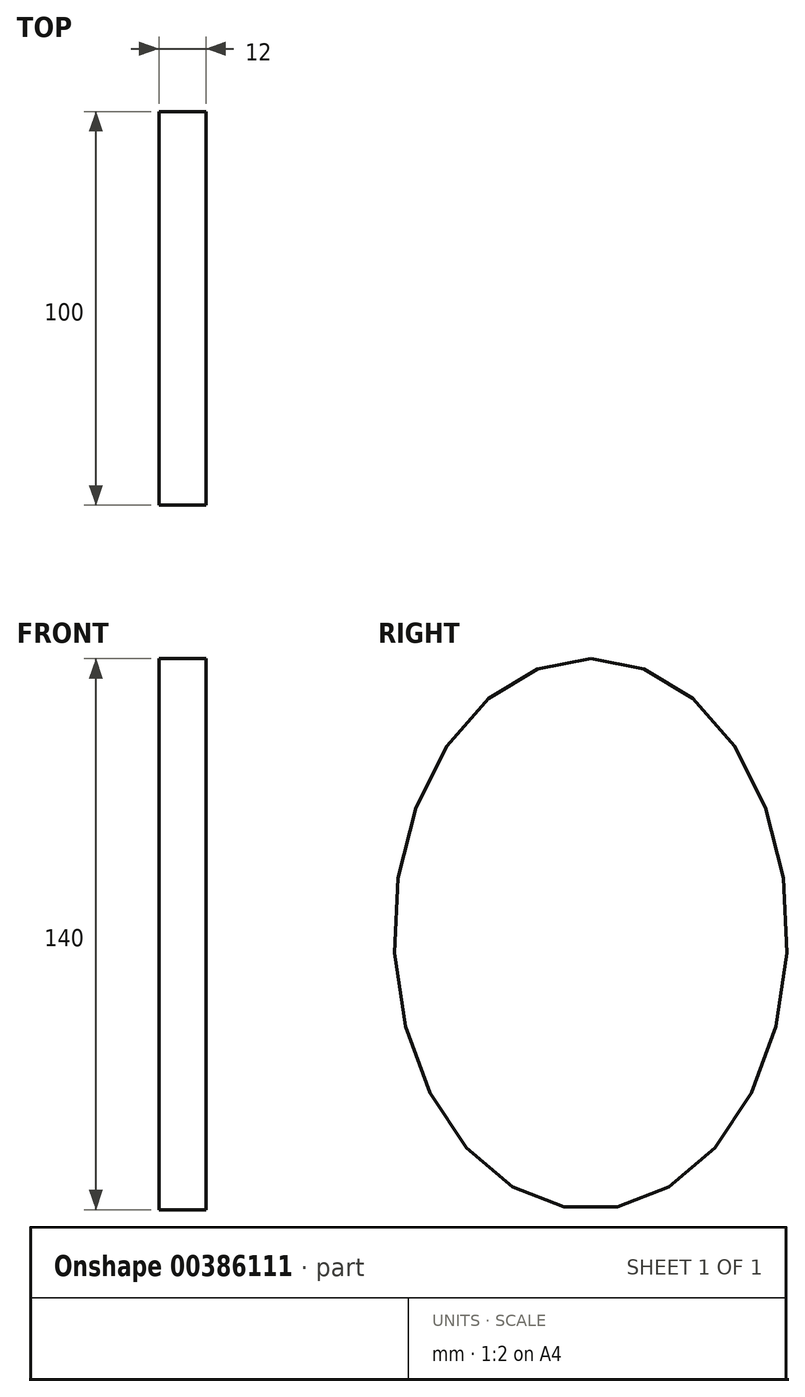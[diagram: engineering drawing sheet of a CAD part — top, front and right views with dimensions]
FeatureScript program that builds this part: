
annotation { "Feature Type Name" : "Feature", "Feature Type Description" : "" }
export const myFeature = defineFeature(function(context is Context, id is Id, definition is map)
    precondition{}
    {
        {
            var Q0;
            Q0=qCreatedBy(makeId("Right.planeOp"),FACE);
            var sketch = newSketch(context, id + "F0", { "sketchPlane" : qUnion([Q0])});
            skEllipse(sketch, "E0", {"center": v(0, 0) * mm, "majorRadius": 70 * mm, "minorRadius": 50 * mm, "majorAxis": v(0, 1)});
            skSolve(sketch);
        }
        {
            var Q0;
            Q0 = qSketchRegion(id + "F0", true);
            extrude(context, id + "F1", {"entities" : qUnion([Q0]), "depth" : 3 * mm});
        }
        {
            var Q0;
            Q0=makeQuery(id+"F1.opExtrude","CAP_FACE",FACE,{"disambiguationData":[OSD([sQuery(id+"F0.wireOp",EDGE,"E0")])],"isStart":false});
            extrude(context, id + "F2", {"entities" : qUnion([Q0]), "operationType" : NewBodyOperationType.ADD, "depth" : 9 * mm});
        }
    });
